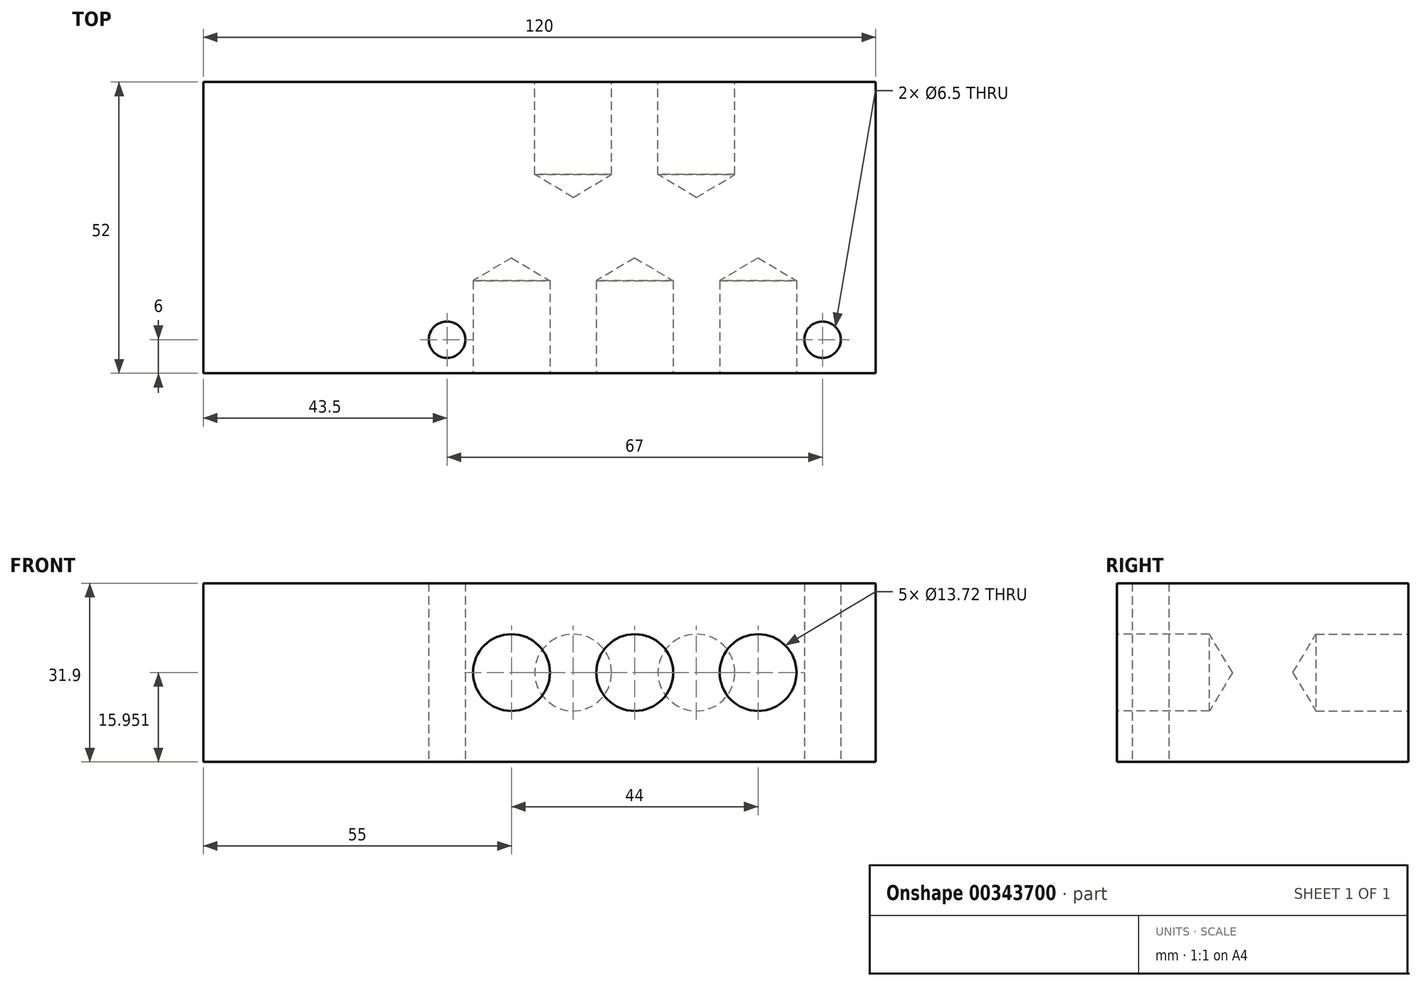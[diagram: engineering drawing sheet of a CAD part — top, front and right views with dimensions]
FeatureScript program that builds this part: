
annotation { "Feature Type Name" : "Feature", "Feature Type Description" : "" }
export const myFeature = defineFeature(function(context is Context, id is Id, definition is map)
    precondition{}
    {
        {
            var Q0;
            Q0=qCreatedBy(makeId("Top.planeOp"),FACE);
            var sketch = newSketch(context, id + "F0", { "sketchPlane" : qUnion([Q0])});
            skLineSegment(sketch, "E0.bottom", {"start": v(60, -26) * mm, "end": v(-60, -26) * mm});
            skLineSegment(sketch, "E0.top", {"start": v(60, 26) * mm, "end": v(-60, 26) * mm});
            skLineSegment(sketch, "E0.left", {"start": v(60, -26) * mm, "end": v(60, 26) * mm});
            skLineSegment(sketch, "E0.right", {"start": v(-60, -26) * mm, "end": v(-60, 26) * mm});
            skPoint(sketch, "E0.middle", {"position": v(0, 0) * mm});
            skLineSegment(sketch, "E1", {"start": v(-60, -20) * mm, "end": v(60, -20) * mm});
            skLineSegment(sketch, "E2", {"start": v(50.5, -26) * mm, "end": v(50.5, 26) * mm});
            skLineSegment(sketch, "E3", {"start": v(-16.5, -26) * mm, "end": v(-16.5, 26) * mm});
            skPoint(sketch, "E4", {"position": v(-16.5, -20) * mm});
            skPoint(sketch, "E5", {"position": v(50.5, -20) * mm});
            skSolve(sketch);
        }
        {
            var Q0;
            Q0 = qSketchRegion(id + "F0", true);
            extrude(context, id + "F1", {"entities" : qUnion([Q0]), "depth" : 31.9 * mm});
        }
        {
            var Q0;
            Q0=sQuery(id+"F0.wireOp",VERTEX,"E4");
            var Q1;
            Q1=sQuery(id+"F0.wireOp",VERTEX,"E5");
            var Q2;
            Q2=makeQuery(id+"F1.opExtrude","SWEPT_BODY",BODY,{"disambiguationData":[OSD([sQuery(id+"F0.wireOp",EDGE,"E0.bottom"),sQuery(id+"F0.wireOp",EDGE,"E0.top"),sQuery(id+"F0.wireOp",EDGE,"E0.left"),sQuery(id+"F0.wireOp",EDGE,"E0.right")])]});
            hole(context, id + "F2", {"style" : HoleStyle.SIMPLE, "endStyle" : HoleEndStyle.THROUGH, "oppositeDirection" : true, "standardTappedOrClearance" : lookupTablePath({ "standard" : "ISO", "size" : "6.5", "type" : "Drilled" }), "standardBlindInLast" : lookupTablePath({ "standard" : "ISO", "size" : "6.5", "type" : "Drilled" }), "holeDiameter" : 6.5 * mm, "isTappedThrough" : true, "tappedDepth" : 12 * mm, "tapClearance" : 3, "locations" : qUnion([Q0, Q1]), "scope" : qUnion([Q2])});
        }
        {
            var Q0;
            Q0=makeQuery(id+"F1.opExtrude","SWEPT_FACE",FACE,{"disambiguationData":[OSD([sQuery(id+"F0.wireOp",EDGE,"E0.bottom")])]});
            var sketch = newSketch(context, id + "F3", { "sketchPlane" : qUnion([Q0])});
            skLineSegment(sketch, "E6", {"start": v(-5, 31.9) * mm, "end": v(-5, 0) * mm});
            skLineSegment(sketch, "E7", {"start": v(17, 31.9) * mm, "end": v(17, 0) * mm});
            skLineSegment(sketch, "E8", {"start": v(39, 31.9) * mm, "end": v(39, 0) * mm});
            skLineSegment(sketch, "E9", {"start": v(-60, 15.95) * mm, "end": v(60, 15.95) * mm});
            skPoint(sketch, "E10", {"position": v(-5, 15.95) * mm});
            skPoint(sketch, "E11", {"position": v(17, 15.95) * mm});
            skPoint(sketch, "E12", {"position": v(39, 15.95) * mm});
            skSolve(sketch);
        }
        {
            var Q0;
            Q0=makeQuery(id+"F1.opExtrude","SWEPT_FACE",FACE,{"disambiguationData":[OSD([sQuery(id+"F0.wireOp",EDGE,"E0.top")])]});
            var sketch = newSketch(context, id + "F4", { "sketchPlane" : qUnion([Q0])});
            skLineSegment(sketch, "E13", {"start": v(60, 15.95) * mm, "end": v(-60, 15.95) * mm});
            skLineSegment(sketch, "E14", {"start": v(-6, 31.9) * mm, "end": v(-6, 0) * mm});
            skLineSegment(sketch, "E15", {"start": v(-28, 31.9) * mm, "end": v(-28, 0) * mm});
            skPoint(sketch, "E16", {"position": v(-28, 15.95) * mm});
            skPoint(sketch, "E17", {"position": v(-6, 15.95) * mm});
            skSolve(sketch);
        }
        {
            var Q0;
            Q0=sQuery(id+"F3.wireOp",VERTEX,"E10");
            var Q1;
            Q1=sQuery(id+"F3.wireOp",VERTEX,"E11");
            var Q2;
            Q2=sQuery(id+"F3.wireOp",VERTEX,"E12");
            var Q3;
            Q3=sQuery(id+"F4.wireOp",VERTEX,"E16");
            var Q4;
            Q4=sQuery(id+"F4.wireOp",VERTEX,"E17");
            var Q5;
            Q5=makeQuery(id+"F1.opExtrude","SWEPT_BODY",BODY,{"disambiguationData":[OSD([sQuery(id+"F0.wireOp",EDGE,"E0.bottom"),sQuery(id+"F0.wireOp",EDGE,"E0.top"),sQuery(id+"F0.wireOp",EDGE,"E0.left"),sQuery(id+"F0.wireOp",EDGE,"E0.right")])]});
            hole(context, id + "F5", {"style" : HoleStyle.SIMPLE, "endStyle" : HoleEndStyle.BLIND, "holeDiameter" : 13.72 * mm, "holeDepth" : 16.5 * mm, "isTappedThrough" : true, "tappedDepth" : 12 * mm, "tapClearance" : 3, "locations" : qUnion([Q0, Q1, Q2, Q3, Q4]), "scope" : qUnion([Q5])});
        }
    });
